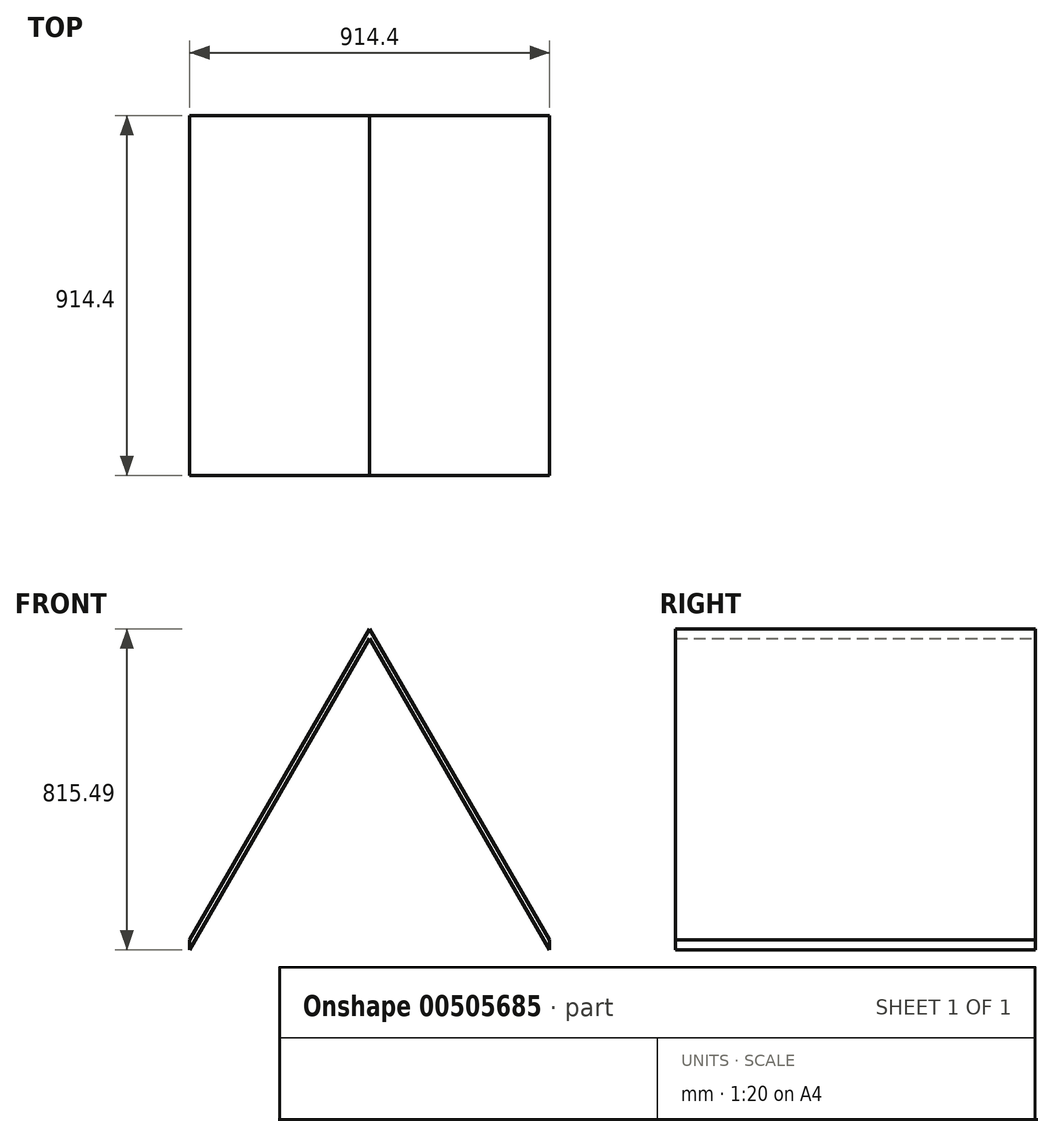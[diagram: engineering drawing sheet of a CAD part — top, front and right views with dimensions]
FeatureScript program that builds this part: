
annotation { "Feature Type Name" : "Feature", "Feature Type Description" : "" }
export const myFeature = defineFeature(function(context is Context, id is Id, definition is map)
    precondition{}
    {
        {
            var Q0;
            Q0=qCreatedBy(makeId("Front.planeOp"),FACE);
            var sketch = newSketch(context, id + "F0", { "sketchPlane" : qUnion([Q0])});
            skLineSegment(sketch, "E0", {"start": v(0, 78.09) * mm, "end": v(-457.2, -712) * mm});
            skLineSegment(sketch, "E1", {"start": v(-457.2, -712) * mm, "end": v(-457.2, -737.4) * mm});
            skLineSegment(sketch, "E2", {"start": v(-457.2, -737.4) * mm, "end": v(0, 54.5) * mm});
            skLineSegment(sketch, "E3", {"start": v(0, 54.5) * mm, "end": v(457.2, -737.4) * mm});
            skLineSegment(sketch, "E4", {"start": v(457.2, -737.4) * mm, "end": v(457.2, -712) * mm});
            skLineSegment(sketch, "E5", {"start": v(457.2, -712) * mm, "end": v(0, 78.09) * mm});
            skSolve(sketch);
        }
        {
            var Q0;
            Q0 = qSketchRegion(id + "F0", true);
            extrude(context, id + "F1", {"entities" : qUnion([Q0]), "depth" : 914.4 * mm});
        }
    });
